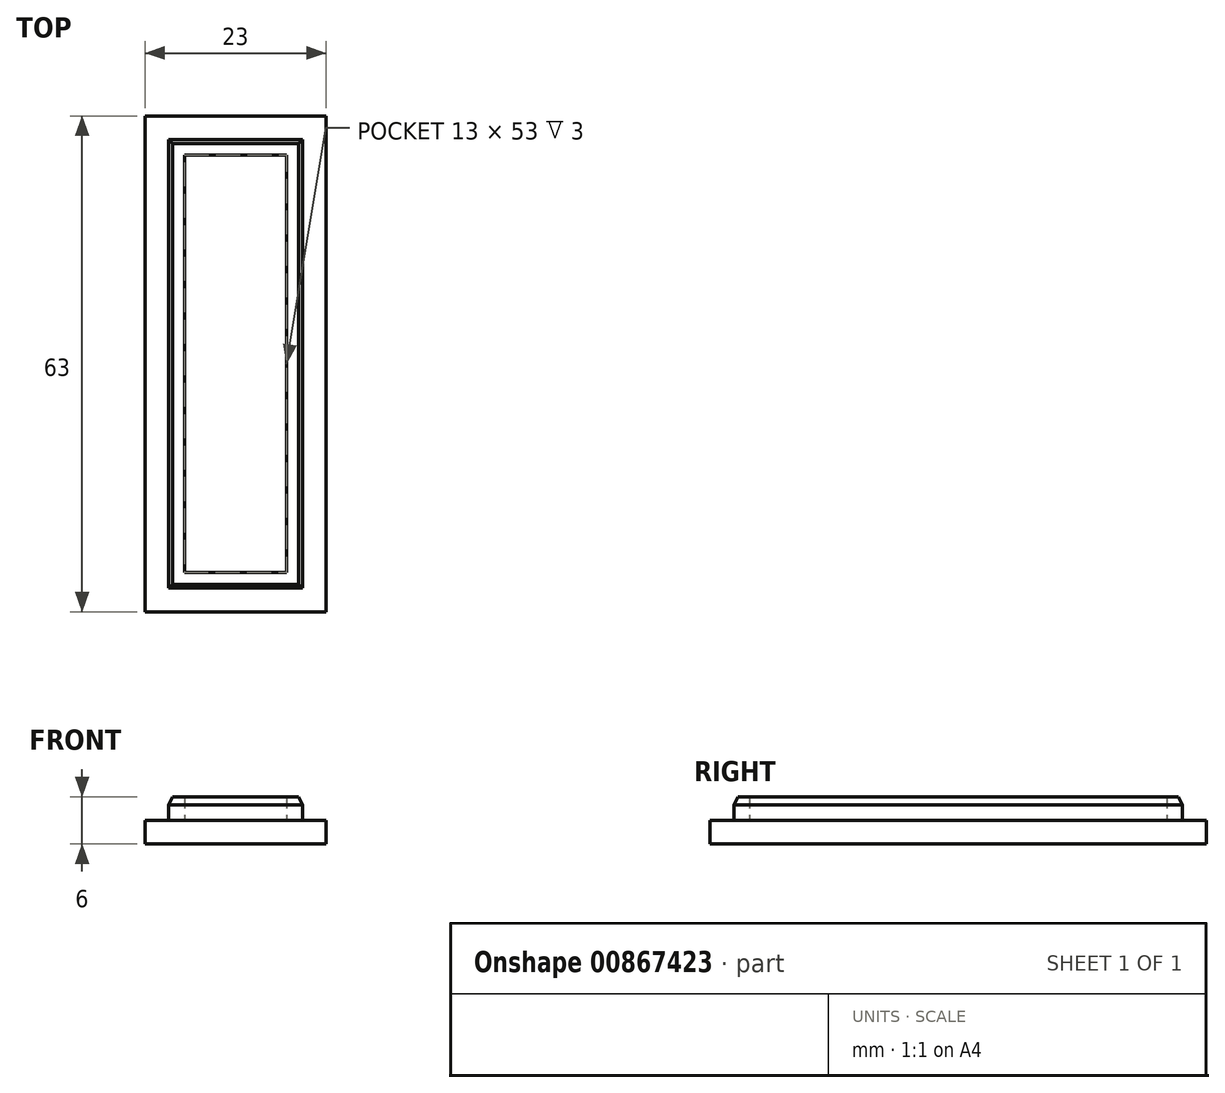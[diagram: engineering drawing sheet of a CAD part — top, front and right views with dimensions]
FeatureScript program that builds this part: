
annotation { "Feature Type Name" : "Feature", "Feature Type Description" : "" }
export const myFeature = defineFeature(function(context is Context, id is Id, definition is map)
    precondition{}
    {
        {
            var Q0;
            Q0=qCreatedBy(makeId("Top.planeOp"),FACE);
            var sketch = newSketch(context, id + "F0", { "sketchPlane" : qUnion([Q0])});
            skLineSegment(sketch, "E0.bottom", {"start": v(0, 0) * mm, "end": v(23, 0) * mm});
            skLineSegment(sketch, "E0.top", {"start": v(0, 63) * mm, "end": v(23, 63) * mm});
            skLineSegment(sketch, "E0.left", {"start": v(0, 0) * mm, "end": v(0, 63) * mm});
            skLineSegment(sketch, "E0.right", {"start": v(23, 0) * mm, "end": v(23, 63) * mm});
            skSolve(sketch);
        }
        {
            var Q0;
            Q0=qSketchRegion(id+"F0",true);
            extrude(context, id + "F1", {"entities" : qUnion([Q0]), "depth" : 3 * mm, "offsetDistance" : 25.4 * mm});
        }
        {
            var Q0;
            Q0=makeQuery(id+"F1.opExtrude","CAP_FACE",FACE,{"disambiguationData":[OSD([sQuery(id+"F0.wireOp",EDGE,"E0.bottom"),sQuery(id+"F0.wireOp",EDGE,"E0.top"),sQuery(id+"F0.wireOp",EDGE,"E0.left"),sQuery(id+"F0.wireOp",EDGE,"E0.right")])],"isStart":true});
            var sketch = newSketch(context, id + "F2", { "sketchPlane" : qUnion([Q0])});
            skLineSegment(sketch, "E1.bottom", {"start": v(20, -60) * mm, "end": v(3, -60) * mm});
            skLineSegment(sketch, "E1.top", {"start": v(20, -3) * mm, "end": v(3, -3) * mm});
            skLineSegment(sketch, "E1.left", {"start": v(20, -60) * mm, "end": v(20, -3) * mm});
            skLineSegment(sketch, "E1.right", {"start": v(3, -60) * mm, "end": v(3, -3) * mm});
            skLineSegment(sketch, "E2.bottom", {"start": v(18, -58) * mm, "end": v(5, -58) * mm});
            skLineSegment(sketch, "E2.top", {"start": v(18, -5) * mm, "end": v(5, -5) * mm});
            skLineSegment(sketch, "E2.left", {"start": v(18, -58) * mm, "end": v(18, -5) * mm});
            skLineSegment(sketch, "E2.right", {"start": v(5, -58) * mm, "end": v(5, -5) * mm});
            skSolve(sketch);
        }
        {
            var Q0;
            Q0=qSketchRegion(id+"F2",true);
            extrude(context, id + "F3", {"entities" : qUnion([Q0]), "operationType" : NewBodyOperationType.ADD, "oppositeDirection" : true, "depth" : 6 * mm, "offsetDistance" : 25.4 * mm});
        }
        {
            var Q0;
            Q0=makeQuery(id+"F3.opExtrude","CAP_EDGE",EDGE,{"disambiguationData":[OSD([sQuery(id+"F2.wireOp",EDGE,"E1.top")])],"isStart":false});
            var Q1;
            Q1=makeQuery(id+"F3.opExtrude","CAP_EDGE",EDGE,{"disambiguationData":[OSD([sQuery(id+"F2.wireOp",EDGE,"E1.left")])],"isStart":false});
            var Q2;
            Q2=makeQuery(id+"F3.opExtrude","CAP_EDGE",EDGE,{"disambiguationData":[OSD([sQuery(id+"F2.wireOp",EDGE,"E1.right")])],"isStart":false});
            var Q3;
            Q3=makeQuery(id+"F3.opExtrude","CAP_EDGE",EDGE,{"disambiguationData":[OSD([sQuery(id+"F2.wireOp",EDGE,"E1.bottom")])],"isStart":false});
            chamfer(context, id + "F4", {"entities" : qUnion([Q0, Q1, Q2, Q3]), "chamferType" : ChamferType.TWO_OFFSETS, "width1" : 1 * mm, "oppositeDirection" : false, "width2" : 0.5 * mm, "tangentPropagation" : true});
        }
    });
